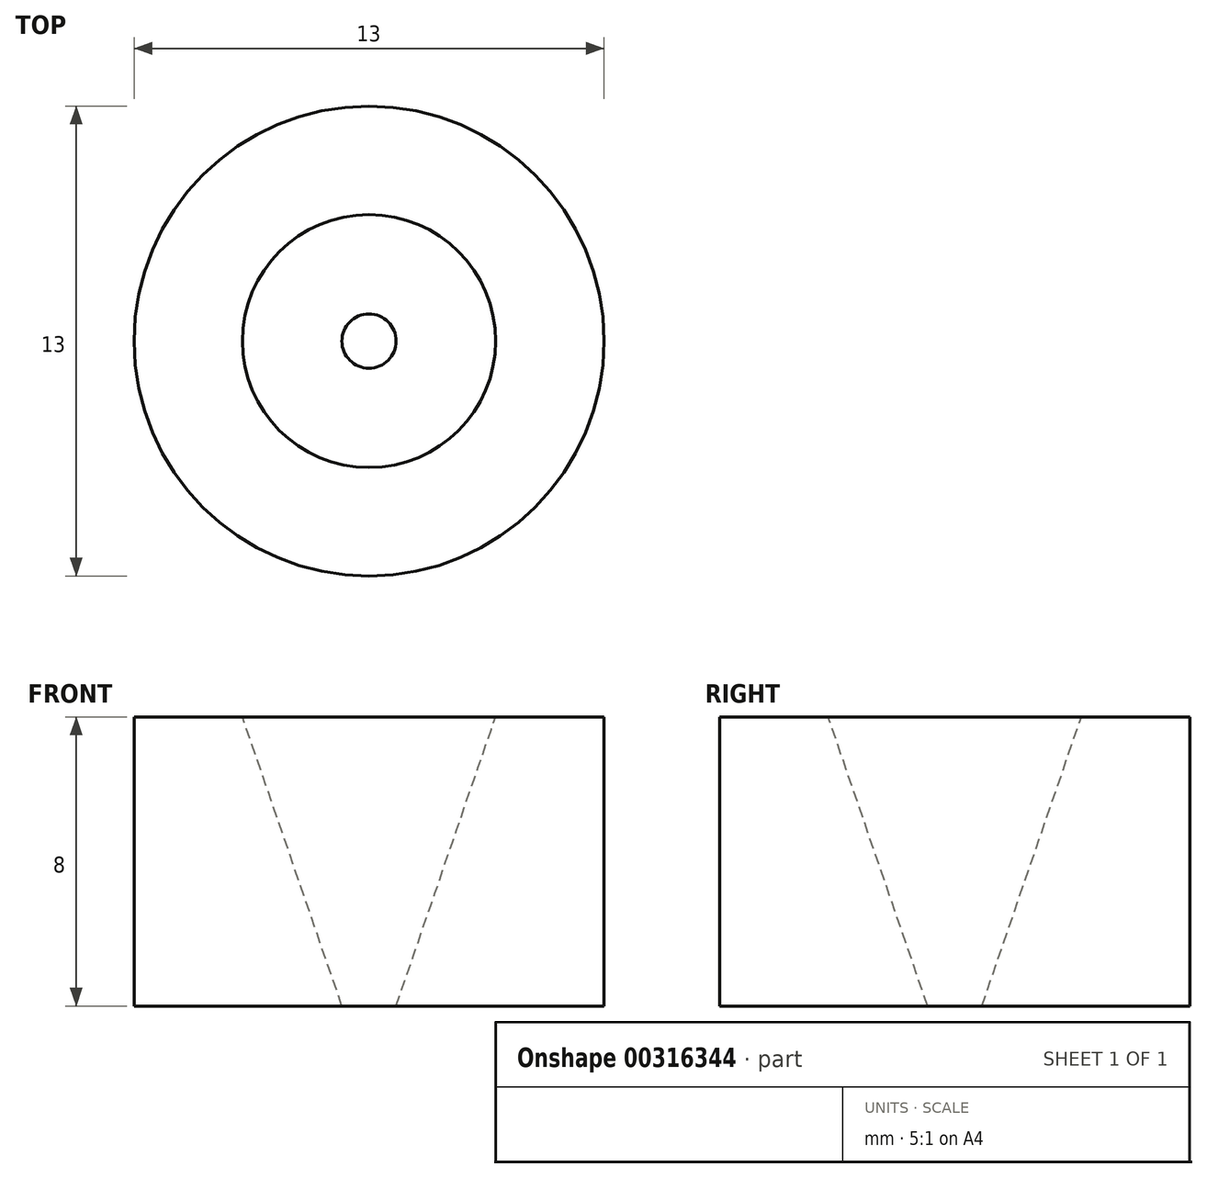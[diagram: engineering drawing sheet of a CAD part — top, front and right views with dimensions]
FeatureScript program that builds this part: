
annotation { "Feature Type Name" : "Feature", "Feature Type Description" : "" }
export const myFeature = defineFeature(function(context is Context, id is Id, definition is map)
    precondition{}
    {
        {
            var Q0;
            Q0=qCreatedBy(makeId("Top.planeOp"),FACE);
            var sketch = newSketch(context, id + "F0", { "sketchPlane" : qUnion([Q0])});
            skCircle(sketch, "E0", {"center": v(0, 0) * mm, "radius": 6.5 * mm});
            skSolve(sketch);
        }
        {
            var Q0;
            Q0 = qSketchRegion(id + "F0", true);
            extrude(context, id + "F1", {"entities" : qUnion([Q0]), "oppositeDirection" : true, "depth" : 8 * mm});
        }
        {
            var Q0;
            Q0=makeQuery(id+"F1.opExtrude","CAP_FACE",FACE,{"disambiguationData":[OSD([sQuery(id+"F0.wireOp",EDGE,"E0")])],"isStart":true});
            var sketch = newSketch(context, id + "F2", { "sketchPlane" : qUnion([Q0])});
            skCircle(sketch, "E1", {"center": v(0, 0) * mm, "radius": 3.5 * mm});
            skSolve(sketch);
        }
        {
            var Q0;
            Q0=makeQuery(id+"F1.opExtrude","CAP_FACE",FACE,{"disambiguationData":[OSD([sQuery(id+"F0.wireOp",EDGE,"E0")])],"isStart":false});
            var sketch = newSketch(context, id + "F3", { "sketchPlane" : qUnion([Q0])});
            skCircle(sketch, "E2", {"center": v(0, 0) * mm, "radius": 0.75 * mm});
            skSolve(sketch);
        }
        {
            var Q1;
            Q1=makeQuery(id+"F3.imprint","IMPRINT",FACE,{"disambiguationData":[TD([[makeQuery(id+"F3.imprint","IMPRINT",EDGE,{"derivedFrom":sQuery(id+"F3.wireOp",EDGE,"E2")}),1.0]])]});
            var Q2;
            Q2 = qSketchRegion(id + "F2", true);
            loft(context, id + "F4", {"operationType" : NewBodyOperationType.REMOVE, "sheetProfilesArray" : [{ "sheetProfileEntities" : qUnion([Q1]) }, { "sheetProfileEntities" : qUnion([Q2]) }]});
        }
    });
